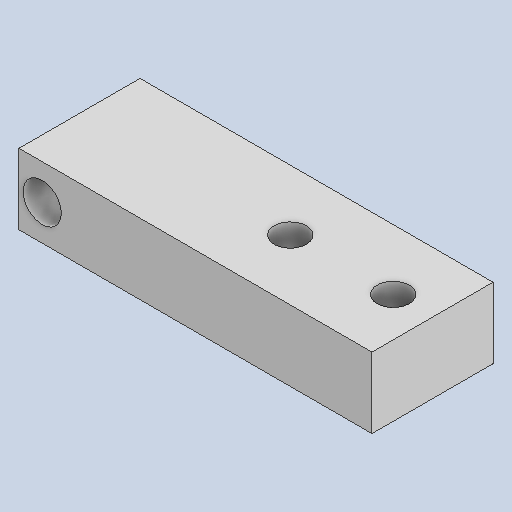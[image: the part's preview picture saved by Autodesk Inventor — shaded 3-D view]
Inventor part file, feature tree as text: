
AUTODESK INVENTOR PART (.ipt)
format: ipt  version: 2024.3 (Build 283343000, 343)  size: 142,336 bytes
history: native  units: mm
features: extrude x2, sketch x2, other x2, reference x1, projected_geometry x1
ambient origin geometry x8: Origin, YZ Plane, XZ Plane, XY Plane, X Axis, Y Axis, Z Axis, Center Point
bodies: Solid1 (feature_tree)
feature tree (8):
  extrude  "Extrusion1"  Depth=7.0mm
  extrude  "Extrusion2"  Depth=12.0mm
  sketch  "Sketch1"  dims[d0=35.0mm d1=7.0mm]
  reference  "Reference1"
  sketch  "Sketch2"  dims[d3=12.0mm d4=0.0mm d5=3.2mm d6=13.4mm d7=1.6mm d8=2.3mm d9=12.0mm d10=0.0mm]
  projected_geometry  "Projected Loop1"
  other  "Assembly1"
  other  "housing:1"
